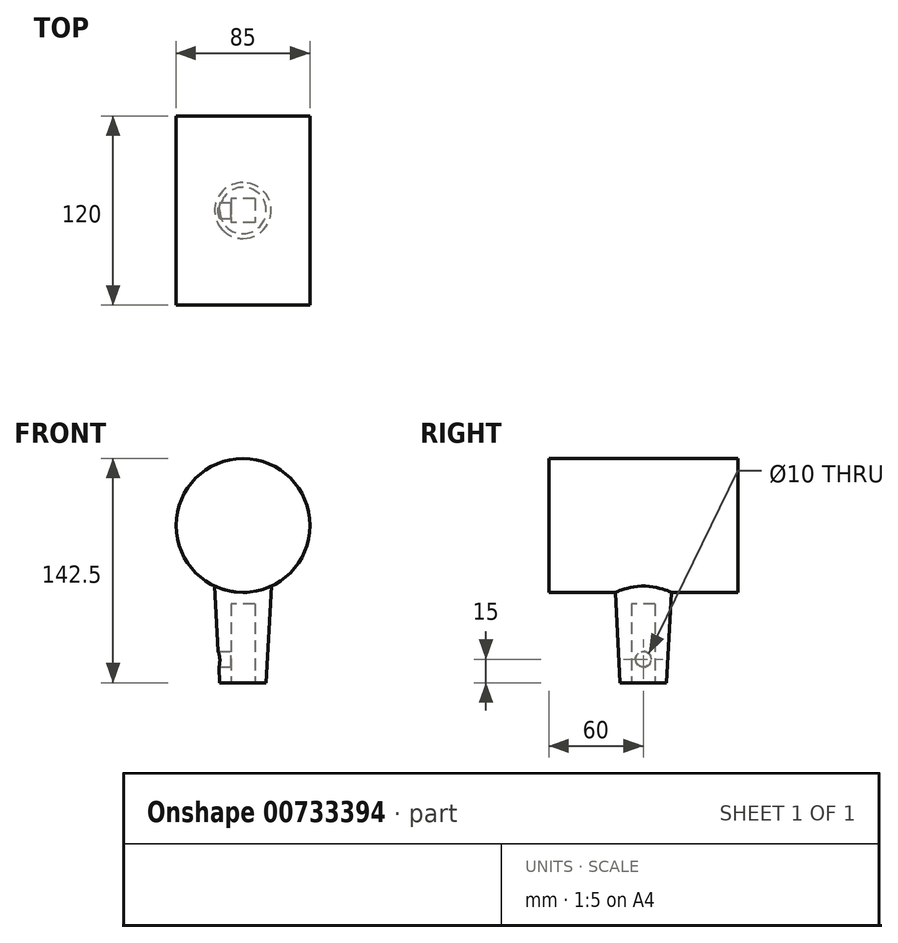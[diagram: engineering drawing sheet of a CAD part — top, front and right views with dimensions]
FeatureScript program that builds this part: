
annotation { "Feature Type Name" : "Feature", "Feature Type Description" : "" }
export const myFeature = defineFeature(function(context is Context, id is Id, definition is map)
    precondition{}
    {
        {
            var Q0;
            Q0=qCreatedBy(makeId("Front.planeOp"),FACE);
            var sketch = newSketch(context, id + "F0", { "sketchPlane" : qUnion([Q0])});
            skCircle(sketch, "E0", {"center": v(0, 0) * mm, "radius": 42.5 * mm});
            skSolve(sketch);
        }
        {
            var Q0;
            Q0=makeQuery(id+"F0.imprint","IMPRINT",FACE,{"disambiguationData":[TD([[makeQuery(id+"F0.imprint","IMPRINT",EDGE,{"derivedFrom":sQuery(id+"F0.wireOp",EDGE,"E0")}),1.0]])]});
            extrude(context, id + "F1", {"entities" : qUnion([Q0]), "endBound" : BoundingType.SYMMETRIC, "depth" : 120 * mm, "offsetDistance" : 25 * mm});
        }
        {
            var Q0;
            Q0=qCreatedBy(makeId("Top.planeOp"),FACE);
            var sketch = newSketch(context, id + "F2", { "sketchPlane" : qUnion([Q0])});
            skCircle(sketch, "E1", {"center": v(0, 0) * mm, "radius": 20 * mm});
            skSolve(sketch);
        }
        {
            var Q0;
            Q0 = qSketchRegion(id + "F2", true);
            extrude(context, id + "F3", {"entities" : qUnion([Q0]), "operationType" : NewBodyOperationType.ADD, "oppositeDirection" : true, "depth" : 100 * mm, "offsetDistance" : 25 * mm, "hasDraft" : true, "draftAngle" : 3 * degree, "draftPullDirection" : true});
        }
        {
            var Q0;
            Q0=makeQuery(id+"F3.opExtrude","CAP_FACE",FACE,{"disambiguationData":[OSD([sQuery(id+"F2.wireOp",EDGE,"E1")])],"isStart":false});
            var sketch = newSketch(context, id + "F4", { "sketchPlane" : qUnion([Q0])});
            skLineSegment(sketch, "E2.bottom", {"start": v(7.5, -7.5) * mm, "end": v(-7.5, -7.5) * mm});
            skLineSegment(sketch, "E2.top", {"start": v(7.5, 7.5) * mm, "end": v(-7.5, 7.5) * mm});
            skLineSegment(sketch, "E2.left", {"start": v(7.5, -7.5) * mm, "end": v(7.5, 7.5) * mm});
            skLineSegment(sketch, "E2.right", {"start": v(-7.5, -7.5) * mm, "end": v(-7.5, 7.5) * mm});
            skPoint(sketch, "E2.middle", {"position": v(0, 0) * mm});
            skSolve(sketch);
        }
        {
            var Q0;
            Q0 = qSketchRegion(id + "F4", true);
            extrude(context, id + "F5", {"entities" : qUnion([Q0]), "operationType" : NewBodyOperationType.REMOVE, "oppositeDirection" : true, "depth" : 50 * mm, "offsetDistance" : 25 * mm});
        }
        {
            var Q0;
            Q0=qCreatedBy(makeId("Right.planeOp"),FACE);
            var sketch = newSketch(context, id + "F6", { "sketchPlane" : qUnion([Q0])});
            skCircle(sketch, "E3", {"center": v(0, -85) * mm, "radius": 5 * mm});
            skSolve(sketch);
        }
        {
            var Q0;
            Q0 = qSketchRegion(id + "F6", true);
            extrude(context, id + "F7", {"entities" : qUnion([Q0]), "operationType" : NewBodyOperationType.REMOVE, "oppositeDirection" : true, "depth" : 50 * mm, "offsetDistance" : 25 * mm});
        }
    });
